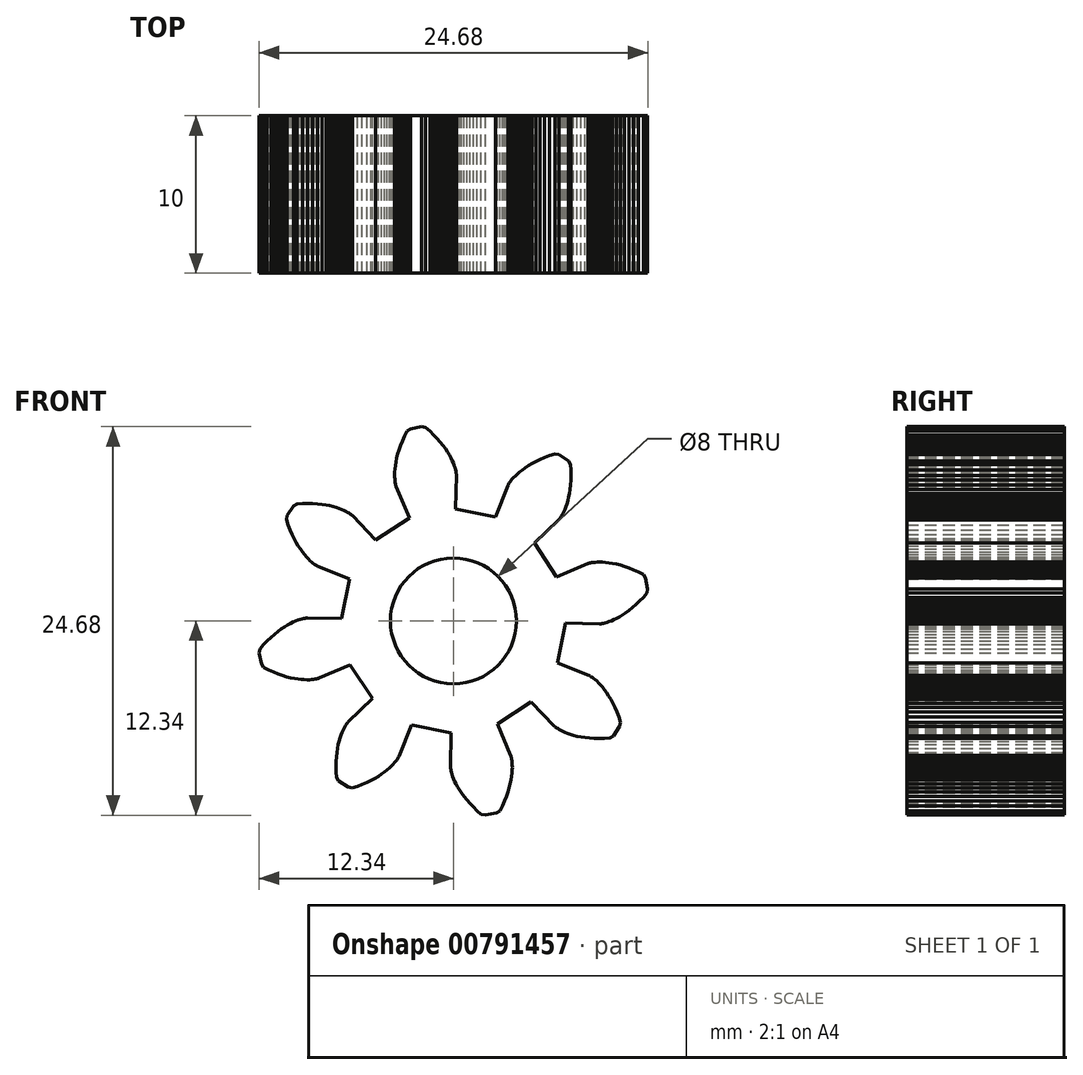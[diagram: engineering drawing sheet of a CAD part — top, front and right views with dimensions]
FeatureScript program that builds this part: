
annotation { "Feature Type Name" : "Feature", "Feature Type Description" : "" }
export const myFeature = defineFeature(function(context is Context, id is Id, definition is map)
    precondition{}
    {
        {
            var Q0;
            Q0=qCreatedBy(makeId("Front.planeOp"),FACE);
            var sketch = newSketch(context, id + "F0", { "sketchPlane" : qUnion([Q0])});
            skCircle(sketch, "E0", {"center": v(0, 0) * mm, "radius": 4 * mm});
            skLineSegment(sketch, "E1", {"start": v(-7.12, 0.14) * mm, "end": v(-9.27, 0.19) * mm});
            skLineSegment(sketch, "E2", {"start": v(-9.27, 0.19) * mm, "end": v(-9.29, 0.19) * mm});
            skLineSegment(sketch, "E3", {"start": v(-9.29, 0.19) * mm, "end": v(-9.32, 0.18) * mm});
            skLineSegment(sketch, "E4", {"start": v(-9.32, 0.18) * mm, "end": v(-9.37, 0.18) * mm});
            skLineSegment(sketch, "E5", {"start": v(-9.37, 0.18) * mm, "end": v(-9.44, 0.17) * mm});
            skLineSegment(sketch, "E6", {"start": v(-9.44, 0.17) * mm, "end": v(-9.52, 0.15) * mm});
            skLineSegment(sketch, "E7", {"start": v(-9.52, 0.15) * mm, "end": v(-9.63, 0.13) * mm});
            skLineSegment(sketch, "E8", {"start": v(-9.63, 0.13) * mm, "end": v(-9.74, 0.1) * mm});
            skLineSegment(sketch, "E9", {"start": v(-9.74, 0.1) * mm, "end": v(-9.87, 0.05) * mm});
            skLineSegment(sketch, "E10", {"start": v(-9.87, 0.05) * mm, "end": v(-10.02, 0) * mm});
            skLineSegment(sketch, "E11", {"start": v(-10.02, 0) * mm, "end": v(-10.18, -0.08) * mm});
            skLineSegment(sketch, "E12", {"start": v(-10.18, -0.08) * mm, "end": v(-10.35, -0.16) * mm});
            skLineSegment(sketch, "E13", {"start": v(-10.35, -0.16) * mm, "end": v(-10.54, -0.26) * mm});
            skLineSegment(sketch, "E14", {"start": v(-10.54, -0.26) * mm, "end": v(-10.73, -0.38) * mm});
            skLineSegment(sketch, "E15", {"start": v(-10.73, -0.38) * mm, "end": v(-10.94, -0.52) * mm});
            skLineSegment(sketch, "E16", {"start": v(-10.94, -0.52) * mm, "end": v(-11.15, -0.67) * mm});
            skLineSegment(sketch, "E17", {"start": v(-11.15, -0.67) * mm, "end": v(-11.37, -0.85) * mm});
            skLineSegment(sketch, "E18", {"start": v(-11.37, -0.85) * mm, "end": v(-11.6, -1.04) * mm});
            skLineSegment(sketch, "E19", {"start": v(-11.6, -1.04) * mm, "end": v(-11.82, -1.26) * mm});
            skLineSegment(sketch, "E20", {"start": v(-11.82, -1.26) * mm, "end": v(-12.05, -1.5) * mm});
            skLineSegment(sketch, "E21", {"start": v(-12.05, -1.5) * mm, "end": v(-12.29, -1.77) * mm});
            skLineSegment(sketch, "E22", {"start": v(-12.29, -1.77) * mm, "end": v(-12.34, -2.02) * mm});
            skLineSegment(sketch, "E23", {"start": v(-12.34, -2.02) * mm, "end": v(-12.2, -2.73) * mm});
            skLineSegment(sketch, "E24", {"start": v(-12.2, -2.73) * mm, "end": v(-12.06, -2.95) * mm});
            skLineSegment(sketch, "E25", {"start": v(-12.06, -2.95) * mm, "end": v(-11.74, -3.11) * mm});
            skLineSegment(sketch, "E26", {"start": v(-11.74, -3.11) * mm, "end": v(-11.44, -3.25) * mm});
            skLineSegment(sketch, "E27", {"start": v(-11.44, -3.25) * mm, "end": v(-11.14, -3.36) * mm});
            skLineSegment(sketch, "E28", {"start": v(-11.14, -3.36) * mm, "end": v(-10.86, -3.46) * mm});
            skLineSegment(sketch, "E29", {"start": v(-10.86, -3.46) * mm, "end": v(-10.6, -3.54) * mm});
            skLineSegment(sketch, "E30", {"start": v(-10.6, -3.54) * mm, "end": v(-10.34, -3.6) * mm});
            skLineSegment(sketch, "E31", {"start": v(-10.34, -3.6) * mm, "end": v(-10.1, -3.66) * mm});
            skLineSegment(sketch, "E32", {"start": v(-10.1, -3.66) * mm, "end": v(-9.87, -3.7) * mm});
            skLineSegment(sketch, "E33", {"start": v(-9.87, -3.7) * mm, "end": v(-9.67, -3.72) * mm});
            skLineSegment(sketch, "E34", {"start": v(-9.67, -3.72) * mm, "end": v(-9.47, -3.73) * mm});
            skLineSegment(sketch, "E35", {"start": v(-9.47, -3.73) * mm, "end": v(-9.3, -3.74) * mm});
            skLineSegment(sketch, "E36", {"start": v(-9.3, -3.74) * mm, "end": v(-9.14, -3.73) * mm});
            skLineSegment(sketch, "E37", {"start": v(-9.14, -3.73) * mm, "end": v(-9, -3.73) * mm});
            skLineSegment(sketch, "E38", {"start": v(-9, -3.73) * mm, "end": v(-8.88, -3.71) * mm});
            skLineSegment(sketch, "E39", {"start": v(-8.88, -3.71) * mm, "end": v(-8.78, -3.7) * mm});
            skLineSegment(sketch, "E40", {"start": v(-8.78, -3.7) * mm, "end": v(-8.7, -3.68) * mm});
            skLineSegment(sketch, "E41", {"start": v(-8.7, -3.68) * mm, "end": v(-8.63, -3.67) * mm});
            skLineSegment(sketch, "E42", {"start": v(-8.63, -3.67) * mm, "end": v(-8.58, -3.65) * mm});
            skLineSegment(sketch, "E43", {"start": v(-8.58, -3.65) * mm, "end": v(-8.55, -3.64) * mm});
            skLineSegment(sketch, "E44", {"start": v(-8.55, -3.64) * mm, "end": v(-8.53, -3.64) * mm});
            skLineSegment(sketch, "E45", {"start": v(-8.53, -3.64) * mm, "end": v(-6.55, -2.8) * mm});
            skLineSegment(sketch, "E46", {"start": v(-6.55, -2.8) * mm, "end": v(-5.14, -4.94) * mm});
            skLineSegment(sketch, "E47", {"start": v(-5.14, -4.94) * mm, "end": v(-6.69, -6.42) * mm});
            skLineSegment(sketch, "E48", {"start": v(-6.69, -6.42) * mm, "end": v(-6.7, -6.44) * mm});
            skLineSegment(sketch, "E49", {"start": v(-6.7, -6.44) * mm, "end": v(-6.72, -6.46) * mm});
            skLineSegment(sketch, "E50", {"start": v(-6.72, -6.46) * mm, "end": v(-6.75, -6.5) * mm});
            skLineSegment(sketch, "E51", {"start": v(-6.75, -6.5) * mm, "end": v(-6.8, -6.56) * mm});
            skLineSegment(sketch, "E52", {"start": v(-6.8, -6.56) * mm, "end": v(-6.84, -6.63) * mm});
            skLineSegment(sketch, "E53", {"start": v(-6.84, -6.63) * mm, "end": v(-6.9, -6.72) * mm});
            skLineSegment(sketch, "E54", {"start": v(-6.9, -6.72) * mm, "end": v(-6.95, -6.82) * mm});
            skLineSegment(sketch, "E55", {"start": v(-6.95, -6.82) * mm, "end": v(-7.02, -6.95) * mm});
            skLineSegment(sketch, "E56", {"start": v(-7.02, -6.95) * mm, "end": v(-7.08, -7.1) * mm});
            skLineSegment(sketch, "E57", {"start": v(-7.08, -7.1) * mm, "end": v(-7.14, -7.25) * mm});
            skLineSegment(sketch, "E58", {"start": v(-7.14, -7.25) * mm, "end": v(-7.2, -7.44) * mm});
            skLineSegment(sketch, "E59", {"start": v(-7.2, -7.44) * mm, "end": v(-7.27, -7.64) * mm});
            skLineSegment(sketch, "E60", {"start": v(-7.27, -7.64) * mm, "end": v(-7.32, -7.86) * mm});
            skLineSegment(sketch, "E61", {"start": v(-7.32, -7.86) * mm, "end": v(-7.37, -8.1) * mm});
            skLineSegment(sketch, "E62", {"start": v(-7.37, -8.1) * mm, "end": v(-7.4, -8.36) * mm});
            skLineSegment(sketch, "E63", {"start": v(-7.4, -8.36) * mm, "end": v(-7.44, -8.64) * mm});
            skLineSegment(sketch, "E64", {"start": v(-7.44, -8.64) * mm, "end": v(-7.46, -8.94) * mm});
            skLineSegment(sketch, "E65", {"start": v(-7.46, -8.94) * mm, "end": v(-7.47, -9.25) * mm});
            skLineSegment(sketch, "E66", {"start": v(-7.47, -9.25) * mm, "end": v(-7.46, -9.59) * mm});
            skLineSegment(sketch, "E67", {"start": v(-7.46, -9.59) * mm, "end": v(-7.44, -9.94) * mm});
            skLineSegment(sketch, "E68", {"start": v(-7.44, -9.94) * mm, "end": v(-7.3, -10.15) * mm});
            skLineSegment(sketch, "E69", {"start": v(-7.3, -10.15) * mm, "end": v(-6.7, -10.56) * mm});
            skLineSegment(sketch, "E70", {"start": v(-6.7, -10.56) * mm, "end": v(-6.44, -10.61) * mm});
            skLineSegment(sketch, "E71", {"start": v(-6.44, -10.61) * mm, "end": v(-6.1, -10.5) * mm});
            skLineSegment(sketch, "E72", {"start": v(-6.1, -10.5) * mm, "end": v(-5.8, -10.38) * mm});
            skLineSegment(sketch, "E73", {"start": v(-5.8, -10.38) * mm, "end": v(-5.5, -10.26) * mm});
            skLineSegment(sketch, "E74", {"start": v(-5.5, -10.26) * mm, "end": v(-5.23, -10.13) * mm});
            skLineSegment(sketch, "E75", {"start": v(-5.23, -10.13) * mm, "end": v(-4.99, -10) * mm});
            skLineSegment(sketch, "E76", {"start": v(-4.99, -10) * mm, "end": v(-4.76, -9.86) * mm});
            skLineSegment(sketch, "E77", {"start": v(-4.76, -9.86) * mm, "end": v(-4.56, -9.73) * mm});
            skLineSegment(sketch, "E78", {"start": v(-4.56, -9.73) * mm, "end": v(-4.37, -9.6) * mm});
            skLineSegment(sketch, "E79", {"start": v(-4.37, -9.6) * mm, "end": v(-4.2, -9.46) * mm});
            skLineSegment(sketch, "E80", {"start": v(-4.2, -9.46) * mm, "end": v(-4.06, -9.34) * mm});
            skLineSegment(sketch, "E81", {"start": v(-4.06, -9.34) * mm, "end": v(-3.93, -9.22) * mm});
            skLineSegment(sketch, "E82", {"start": v(-3.93, -9.22) * mm, "end": v(-3.82, -9.1) * mm});
            skLineSegment(sketch, "E83", {"start": v(-3.82, -9.1) * mm, "end": v(-3.73, -9) * mm});
            skLineSegment(sketch, "E84", {"start": v(-3.73, -9) * mm, "end": v(-3.65, -8.9) * mm});
            skLineSegment(sketch, "E85", {"start": v(-3.65, -8.9) * mm, "end": v(-3.6, -8.82) * mm});
            skLineSegment(sketch, "E86", {"start": v(-3.6, -8.82) * mm, "end": v(-3.54, -8.75) * mm});
            skLineSegment(sketch, "E87", {"start": v(-3.54, -8.75) * mm, "end": v(-3.5, -8.7) * mm});
            skLineSegment(sketch, "E88", {"start": v(-3.5, -8.7) * mm, "end": v(-3.48, -8.65) * mm});
            skLineSegment(sketch, "E89", {"start": v(-3.48, -8.65) * mm, "end": v(-3.47, -8.62) * mm});
            skLineSegment(sketch, "E90", {"start": v(-3.47, -8.62) * mm, "end": v(-3.46, -8.6) * mm});
            skLineSegment(sketch, "E91", {"start": v(-3.46, -8.6) * mm, "end": v(-2.66, -6.61) * mm});
            skLineSegment(sketch, "E92", {"start": v(-2.66, -6.61) * mm, "end": v(-0.14, -7.12) * mm});
            skLineSegment(sketch, "E93", {"start": v(-0.14, -7.12) * mm, "end": v(-0.19, -9.27) * mm});
            skLineSegment(sketch, "E94", {"start": v(-0.19, -9.27) * mm, "end": v(-0.19, -9.29) * mm});
            skLineSegment(sketch, "E95", {"start": v(-0.19, -9.29) * mm, "end": v(-0.18, -9.32) * mm});
            skLineSegment(sketch, "E96", {"start": v(-0.18, -9.32) * mm, "end": v(-0.18, -9.37) * mm});
            skLineSegment(sketch, "E97", {"start": v(-0.18, -9.37) * mm, "end": v(-0.17, -9.44) * mm});
            skLineSegment(sketch, "E98", {"start": v(-0.17, -9.44) * mm, "end": v(-0.15, -9.52) * mm});
            skLineSegment(sketch, "E99", {"start": v(-0.15, -9.52) * mm, "end": v(-0.13, -9.63) * mm});
            skLineSegment(sketch, "E100", {"start": v(-0.13, -9.63) * mm, "end": v(-0.1, -9.74) * mm});
            skLineSegment(sketch, "E101", {"start": v(-0.1, -9.74) * mm, "end": v(-0.05, -9.87) * mm});
            skLineSegment(sketch, "E102", {"start": v(-0.05, -9.87) * mm, "end": v(0, -10.02) * mm});
            skLineSegment(sketch, "E103", {"start": v(0, -10.02) * mm, "end": v(0.08, -10.18) * mm});
            skLineSegment(sketch, "E104", {"start": v(0.08, -10.18) * mm, "end": v(0.16, -10.35) * mm});
            skLineSegment(sketch, "E105", {"start": v(0.16, -10.35) * mm, "end": v(0.26, -10.54) * mm});
            skLineSegment(sketch, "E106", {"start": v(0.26, -10.54) * mm, "end": v(0.38, -10.73) * mm});
            skLineSegment(sketch, "E107", {"start": v(0.38, -10.73) * mm, "end": v(0.52, -10.94) * mm});
            skLineSegment(sketch, "E108", {"start": v(0.52, -10.94) * mm, "end": v(0.67, -11.15) * mm});
            skLineSegment(sketch, "E109", {"start": v(0.67, -11.15) * mm, "end": v(0.85, -11.37) * mm});
            skLineSegment(sketch, "E110", {"start": v(0.85, -11.37) * mm, "end": v(1.04, -11.6) * mm});
            skLineSegment(sketch, "E111", {"start": v(1.04, -11.6) * mm, "end": v(1.26, -11.82) * mm});
            skLineSegment(sketch, "E112", {"start": v(1.26, -11.82) * mm, "end": v(1.5, -12.05) * mm});
            skLineSegment(sketch, "E113", {"start": v(1.5, -12.05) * mm, "end": v(1.77, -12.29) * mm});
            skLineSegment(sketch, "E114", {"start": v(1.77, -12.29) * mm, "end": v(2.02, -12.34) * mm});
            skLineSegment(sketch, "E115", {"start": v(2.02, -12.34) * mm, "end": v(2.73, -12.2) * mm});
            skLineSegment(sketch, "E116", {"start": v(2.73, -12.2) * mm, "end": v(2.95, -12.06) * mm});
            skLineSegment(sketch, "E117", {"start": v(2.95, -12.06) * mm, "end": v(3.11, -11.74) * mm});
            skLineSegment(sketch, "E118", {"start": v(3.11, -11.74) * mm, "end": v(3.25, -11.44) * mm});
            skLineSegment(sketch, "E119", {"start": v(3.25, -11.44) * mm, "end": v(3.36, -11.14) * mm});
            skLineSegment(sketch, "E120", {"start": v(3.36, -11.14) * mm, "end": v(3.46, -10.86) * mm});
            skLineSegment(sketch, "E121", {"start": v(3.46, -10.86) * mm, "end": v(3.54, -10.6) * mm});
            skLineSegment(sketch, "E122", {"start": v(3.54, -10.6) * mm, "end": v(3.6, -10.34) * mm});
            skLineSegment(sketch, "E123", {"start": v(3.6, -10.34) * mm, "end": v(3.66, -10.1) * mm});
            skLineSegment(sketch, "E124", {"start": v(3.66, -10.1) * mm, "end": v(3.7, -9.87) * mm});
            skLineSegment(sketch, "E125", {"start": v(3.7, -9.87) * mm, "end": v(3.72, -9.67) * mm});
            skLineSegment(sketch, "E126", {"start": v(3.72, -9.67) * mm, "end": v(3.73, -9.47) * mm});
            skLineSegment(sketch, "E127", {"start": v(3.73, -9.47) * mm, "end": v(3.74, -9.3) * mm});
            skLineSegment(sketch, "E128", {"start": v(3.74, -9.3) * mm, "end": v(3.73, -9.14) * mm});
            skLineSegment(sketch, "E129", {"start": v(3.73, -9.14) * mm, "end": v(3.73, -9) * mm});
            skLineSegment(sketch, "E130", {"start": v(3.73, -9) * mm, "end": v(3.71, -8.88) * mm});
            skLineSegment(sketch, "E131", {"start": v(3.71, -8.88) * mm, "end": v(3.7, -8.78) * mm});
            skLineSegment(sketch, "E132", {"start": v(3.7, -8.78) * mm, "end": v(3.68, -8.7) * mm});
            skLineSegment(sketch, "E133", {"start": v(3.68, -8.7) * mm, "end": v(3.67, -8.63) * mm});
            skLineSegment(sketch, "E134", {"start": v(3.67, -8.63) * mm, "end": v(3.65, -8.58) * mm});
            skLineSegment(sketch, "E135", {"start": v(3.65, -8.58) * mm, "end": v(3.64, -8.55) * mm});
            skLineSegment(sketch, "E136", {"start": v(3.64, -8.55) * mm, "end": v(3.64, -8.53) * mm});
            skLineSegment(sketch, "E137", {"start": v(3.64, -8.53) * mm, "end": v(2.8, -6.55) * mm});
            skLineSegment(sketch, "E138", {"start": v(2.8, -6.55) * mm, "end": v(4.94, -5.14) * mm});
            skLineSegment(sketch, "E139", {"start": v(4.94, -5.14) * mm, "end": v(6.42, -6.69) * mm});
            skLineSegment(sketch, "E140", {"start": v(6.42, -6.69) * mm, "end": v(6.44, -6.7) * mm});
            skLineSegment(sketch, "E141", {"start": v(6.44, -6.7) * mm, "end": v(6.46, -6.72) * mm});
            skLineSegment(sketch, "E142", {"start": v(6.46, -6.72) * mm, "end": v(6.5, -6.75) * mm});
            skLineSegment(sketch, "E143", {"start": v(6.5, -6.75) * mm, "end": v(6.56, -6.8) * mm});
            skLineSegment(sketch, "E144", {"start": v(6.56, -6.8) * mm, "end": v(6.63, -6.84) * mm});
            skLineSegment(sketch, "E145", {"start": v(6.63, -6.84) * mm, "end": v(6.72, -6.9) * mm});
            skLineSegment(sketch, "E146", {"start": v(6.72, -6.9) * mm, "end": v(6.82, -6.95) * mm});
            skLineSegment(sketch, "E147", {"start": v(6.82, -6.95) * mm, "end": v(6.95, -7.02) * mm});
            skLineSegment(sketch, "E148", {"start": v(6.95, -7.02) * mm, "end": v(7.1, -7.08) * mm});
            skLineSegment(sketch, "E149", {"start": v(7.1, -7.08) * mm, "end": v(7.25, -7.14) * mm});
            skLineSegment(sketch, "E150", {"start": v(7.25, -7.14) * mm, "end": v(7.44, -7.2) * mm});
            skLineSegment(sketch, "E151", {"start": v(7.44, -7.2) * mm, "end": v(7.64, -7.27) * mm});
            skLineSegment(sketch, "E152", {"start": v(7.64, -7.27) * mm, "end": v(7.86, -7.32) * mm});
            skLineSegment(sketch, "E153", {"start": v(7.86, -7.32) * mm, "end": v(8.1, -7.37) * mm});
            skLineSegment(sketch, "E154", {"start": v(8.1, -7.37) * mm, "end": v(8.36, -7.4) * mm});
            skLineSegment(sketch, "E155", {"start": v(8.36, -7.4) * mm, "end": v(8.64, -7.44) * mm});
            skLineSegment(sketch, "E156", {"start": v(8.64, -7.44) * mm, "end": v(8.94, -7.46) * mm});
            skLineSegment(sketch, "E157", {"start": v(8.94, -7.46) * mm, "end": v(9.25, -7.47) * mm});
            skLineSegment(sketch, "E158", {"start": v(9.25, -7.47) * mm, "end": v(9.59, -7.46) * mm});
            skLineSegment(sketch, "E159", {"start": v(9.59, -7.46) * mm, "end": v(9.94, -7.44) * mm});
            skLineSegment(sketch, "E160", {"start": v(9.94, -7.44) * mm, "end": v(10.15, -7.3) * mm});
            skLineSegment(sketch, "E161", {"start": v(10.15, -7.3) * mm, "end": v(10.56, -6.7) * mm});
            skLineSegment(sketch, "E162", {"start": v(10.56, -6.7) * mm, "end": v(10.61, -6.44) * mm});
            skLineSegment(sketch, "E163", {"start": v(10.61, -6.44) * mm, "end": v(10.5, -6.1) * mm});
            skLineSegment(sketch, "E164", {"start": v(10.5, -6.1) * mm, "end": v(10.38, -5.8) * mm});
            skLineSegment(sketch, "E165", {"start": v(10.38, -5.8) * mm, "end": v(10.26, -5.5) * mm});
            skLineSegment(sketch, "E166", {"start": v(10.26, -5.5) * mm, "end": v(10.13, -5.23) * mm});
            skLineSegment(sketch, "E167", {"start": v(10.13, -5.23) * mm, "end": v(10, -4.99) * mm});
            skLineSegment(sketch, "E168", {"start": v(10, -4.99) * mm, "end": v(9.86, -4.76) * mm});
            skLineSegment(sketch, "E169", {"start": v(9.86, -4.76) * mm, "end": v(9.73, -4.56) * mm});
            skLineSegment(sketch, "E170", {"start": v(9.73, -4.56) * mm, "end": v(9.6, -4.37) * mm});
            skLineSegment(sketch, "E171", {"start": v(9.6, -4.37) * mm, "end": v(9.46, -4.2) * mm});
            skLineSegment(sketch, "E172", {"start": v(9.46, -4.2) * mm, "end": v(9.34, -4.06) * mm});
            skLineSegment(sketch, "E173", {"start": v(9.34, -4.06) * mm, "end": v(9.22, -3.93) * mm});
            skLineSegment(sketch, "E174", {"start": v(9.22, -3.93) * mm, "end": v(9.1, -3.82) * mm});
            skLineSegment(sketch, "E175", {"start": v(9.1, -3.82) * mm, "end": v(9, -3.73) * mm});
            skLineSegment(sketch, "E176", {"start": v(9, -3.73) * mm, "end": v(8.9, -3.65) * mm});
            skLineSegment(sketch, "E177", {"start": v(8.9, -3.65) * mm, "end": v(8.82, -3.6) * mm});
            skLineSegment(sketch, "E178", {"start": v(8.82, -3.6) * mm, "end": v(8.75, -3.54) * mm});
            skLineSegment(sketch, "E179", {"start": v(8.75, -3.54) * mm, "end": v(8.7, -3.5) * mm});
            skLineSegment(sketch, "E180", {"start": v(8.7, -3.5) * mm, "end": v(8.65, -3.48) * mm});
            skLineSegment(sketch, "E181", {"start": v(8.65, -3.48) * mm, "end": v(8.62, -3.47) * mm});
            skLineSegment(sketch, "E182", {"start": v(8.62, -3.47) * mm, "end": v(8.6, -3.46) * mm});
            skLineSegment(sketch, "E183", {"start": v(8.6, -3.46) * mm, "end": v(6.61, -2.66) * mm});
            skLineSegment(sketch, "E184", {"start": v(6.61, -2.66) * mm, "end": v(7.12, -0.14) * mm});
            skLineSegment(sketch, "E185", {"start": v(7.12, -0.14) * mm, "end": v(9.27, -0.19) * mm});
            skLineSegment(sketch, "E186", {"start": v(9.27, -0.19) * mm, "end": v(9.29, -0.19) * mm});
            skLineSegment(sketch, "E187", {"start": v(9.29, -0.19) * mm, "end": v(9.32, -0.18) * mm});
            skLineSegment(sketch, "E188", {"start": v(9.32, -0.18) * mm, "end": v(9.37, -0.18) * mm});
            skLineSegment(sketch, "E189", {"start": v(9.37, -0.18) * mm, "end": v(9.44, -0.17) * mm});
            skLineSegment(sketch, "E190", {"start": v(9.44, -0.17) * mm, "end": v(9.52, -0.15) * mm});
            skLineSegment(sketch, "E191", {"start": v(9.52, -0.15) * mm, "end": v(9.63, -0.13) * mm});
            skLineSegment(sketch, "E192", {"start": v(9.63, -0.13) * mm, "end": v(9.74, -0.1) * mm});
            skLineSegment(sketch, "E193", {"start": v(9.74, -0.1) * mm, "end": v(9.87, -0.05) * mm});
            skLineSegment(sketch, "E194", {"start": v(9.87, -0.05) * mm, "end": v(10.02, 0) * mm});
            skLineSegment(sketch, "E195", {"start": v(10.02, 0) * mm, "end": v(10.18, 0.08) * mm});
            skLineSegment(sketch, "E196", {"start": v(10.18, 0.08) * mm, "end": v(10.35, 0.16) * mm});
            skLineSegment(sketch, "E197", {"start": v(10.35, 0.16) * mm, "end": v(10.54, 0.26) * mm});
            skLineSegment(sketch, "E198", {"start": v(10.54, 0.26) * mm, "end": v(10.73, 0.38) * mm});
            skLineSegment(sketch, "E199", {"start": v(10.73, 0.38) * mm, "end": v(10.94, 0.52) * mm});
            skLineSegment(sketch, "E200", {"start": v(10.94, 0.52) * mm, "end": v(11.15, 0.67) * mm});
            skLineSegment(sketch, "E201", {"start": v(11.15, 0.67) * mm, "end": v(11.37, 0.85) * mm});
            skLineSegment(sketch, "E202", {"start": v(11.37, 0.85) * mm, "end": v(11.6, 1.04) * mm});
            skLineSegment(sketch, "E203", {"start": v(11.6, 1.04) * mm, "end": v(11.82, 1.26) * mm});
            skLineSegment(sketch, "E204", {"start": v(11.82, 1.26) * mm, "end": v(12.05, 1.5) * mm});
            skLineSegment(sketch, "E205", {"start": v(12.05, 1.5) * mm, "end": v(12.29, 1.77) * mm});
            skLineSegment(sketch, "E206", {"start": v(12.29, 1.77) * mm, "end": v(12.34, 2.02) * mm});
            skLineSegment(sketch, "E207", {"start": v(12.34, 2.02) * mm, "end": v(12.2, 2.73) * mm});
            skLineSegment(sketch, "E208", {"start": v(12.2, 2.73) * mm, "end": v(12.06, 2.95) * mm});
            skLineSegment(sketch, "E209", {"start": v(12.06, 2.95) * mm, "end": v(11.74, 3.11) * mm});
            skLineSegment(sketch, "E210", {"start": v(11.74, 3.11) * mm, "end": v(11.44, 3.25) * mm});
            skLineSegment(sketch, "E211", {"start": v(11.44, 3.25) * mm, "end": v(11.14, 3.36) * mm});
            skLineSegment(sketch, "E212", {"start": v(11.14, 3.36) * mm, "end": v(10.86, 3.46) * mm});
            skLineSegment(sketch, "E213", {"start": v(10.86, 3.46) * mm, "end": v(10.6, 3.54) * mm});
            skLineSegment(sketch, "E214", {"start": v(10.6, 3.54) * mm, "end": v(10.34, 3.6) * mm});
            skLineSegment(sketch, "E215", {"start": v(10.34, 3.6) * mm, "end": v(10.1, 3.66) * mm});
            skLineSegment(sketch, "E216", {"start": v(10.1, 3.66) * mm, "end": v(9.87, 3.7) * mm});
            skLineSegment(sketch, "E217", {"start": v(9.87, 3.7) * mm, "end": v(9.67, 3.72) * mm});
            skLineSegment(sketch, "E218", {"start": v(9.67, 3.72) * mm, "end": v(9.47, 3.73) * mm});
            skLineSegment(sketch, "E219", {"start": v(9.47, 3.73) * mm, "end": v(9.3, 3.74) * mm});
            skLineSegment(sketch, "E220", {"start": v(9.3, 3.74) * mm, "end": v(9.14, 3.73) * mm});
            skLineSegment(sketch, "E221", {"start": v(9.14, 3.73) * mm, "end": v(9, 3.73) * mm});
            skLineSegment(sketch, "E222", {"start": v(9, 3.73) * mm, "end": v(8.88, 3.71) * mm});
            skLineSegment(sketch, "E223", {"start": v(8.88, 3.71) * mm, "end": v(8.78, 3.7) * mm});
            skLineSegment(sketch, "E224", {"start": v(8.78, 3.7) * mm, "end": v(8.7, 3.68) * mm});
            skLineSegment(sketch, "E225", {"start": v(8.7, 3.68) * mm, "end": v(8.63, 3.67) * mm});
            skLineSegment(sketch, "E226", {"start": v(8.63, 3.67) * mm, "end": v(8.58, 3.65) * mm});
            skLineSegment(sketch, "E227", {"start": v(8.58, 3.65) * mm, "end": v(8.55, 3.64) * mm});
            skLineSegment(sketch, "E228", {"start": v(8.55, 3.64) * mm, "end": v(8.53, 3.64) * mm});
            skLineSegment(sketch, "E229", {"start": v(8.53, 3.64) * mm, "end": v(6.55, 2.8) * mm});
            skLineSegment(sketch, "E230", {"start": v(6.55, 2.8) * mm, "end": v(5.14, 4.94) * mm});
            skLineSegment(sketch, "E231", {"start": v(5.14, 4.94) * mm, "end": v(6.69, 6.42) * mm});
            skLineSegment(sketch, "E232", {"start": v(6.69, 6.42) * mm, "end": v(6.7, 6.44) * mm});
            skLineSegment(sketch, "E233", {"start": v(6.7, 6.44) * mm, "end": v(6.72, 6.46) * mm});
            skLineSegment(sketch, "E234", {"start": v(6.72, 6.46) * mm, "end": v(6.75, 6.5) * mm});
            skLineSegment(sketch, "E235", {"start": v(6.75, 6.5) * mm, "end": v(6.8, 6.56) * mm});
            skLineSegment(sketch, "E236", {"start": v(6.8, 6.56) * mm, "end": v(6.84, 6.63) * mm});
            skLineSegment(sketch, "E237", {"start": v(6.84, 6.63) * mm, "end": v(6.9, 6.72) * mm});
            skLineSegment(sketch, "E238", {"start": v(6.9, 6.72) * mm, "end": v(6.95, 6.82) * mm});
            skLineSegment(sketch, "E239", {"start": v(6.95, 6.82) * mm, "end": v(7.02, 6.95) * mm});
            skLineSegment(sketch, "E240", {"start": v(7.02, 6.95) * mm, "end": v(7.08, 7.1) * mm});
            skLineSegment(sketch, "E241", {"start": v(7.08, 7.1) * mm, "end": v(7.14, 7.25) * mm});
            skLineSegment(sketch, "E242", {"start": v(7.14, 7.25) * mm, "end": v(7.2, 7.44) * mm});
            skLineSegment(sketch, "E243", {"start": v(7.2, 7.44) * mm, "end": v(7.27, 7.64) * mm});
            skLineSegment(sketch, "E244", {"start": v(7.27, 7.64) * mm, "end": v(7.32, 7.86) * mm});
            skLineSegment(sketch, "E245", {"start": v(7.32, 7.86) * mm, "end": v(7.37, 8.1) * mm});
            skLineSegment(sketch, "E246", {"start": v(7.37, 8.1) * mm, "end": v(7.4, 8.36) * mm});
            skLineSegment(sketch, "E247", {"start": v(7.4, 8.36) * mm, "end": v(7.44, 8.64) * mm});
            skLineSegment(sketch, "E248", {"start": v(7.44, 8.64) * mm, "end": v(7.46, 8.94) * mm});
            skLineSegment(sketch, "E249", {"start": v(7.46, 8.94) * mm, "end": v(7.47, 9.25) * mm});
            skLineSegment(sketch, "E250", {"start": v(7.47, 9.25) * mm, "end": v(7.46, 9.59) * mm});
            skLineSegment(sketch, "E251", {"start": v(7.46, 9.59) * mm, "end": v(7.44, 9.94) * mm});
            skLineSegment(sketch, "E252", {"start": v(7.44, 9.94) * mm, "end": v(7.3, 10.15) * mm});
            skLineSegment(sketch, "E253", {"start": v(7.3, 10.15) * mm, "end": v(6.7, 10.56) * mm});
            skLineSegment(sketch, "E254", {"start": v(6.7, 10.56) * mm, "end": v(6.44, 10.61) * mm});
            skLineSegment(sketch, "E255", {"start": v(6.44, 10.61) * mm, "end": v(6.1, 10.5) * mm});
            skLineSegment(sketch, "E256", {"start": v(6.1, 10.5) * mm, "end": v(5.8, 10.38) * mm});
            skLineSegment(sketch, "E257", {"start": v(5.8, 10.38) * mm, "end": v(5.5, 10.26) * mm});
            skLineSegment(sketch, "E258", {"start": v(5.5, 10.26) * mm, "end": v(5.23, 10.13) * mm});
            skLineSegment(sketch, "E259", {"start": v(5.23, 10.13) * mm, "end": v(4.99, 10) * mm});
            skLineSegment(sketch, "E260", {"start": v(4.99, 10) * mm, "end": v(4.76, 9.86) * mm});
            skLineSegment(sketch, "E261", {"start": v(4.76, 9.86) * mm, "end": v(4.56, 9.73) * mm});
            skLineSegment(sketch, "E262", {"start": v(4.56, 9.73) * mm, "end": v(4.37, 9.6) * mm});
            skLineSegment(sketch, "E263", {"start": v(4.37, 9.6) * mm, "end": v(4.2, 9.46) * mm});
            skLineSegment(sketch, "E264", {"start": v(4.2, 9.46) * mm, "end": v(4.06, 9.34) * mm});
            skLineSegment(sketch, "E265", {"start": v(4.06, 9.34) * mm, "end": v(3.93, 9.22) * mm});
            skLineSegment(sketch, "E266", {"start": v(3.93, 9.22) * mm, "end": v(3.82, 9.1) * mm});
            skLineSegment(sketch, "E267", {"start": v(3.82, 9.1) * mm, "end": v(3.73, 9) * mm});
            skLineSegment(sketch, "E268", {"start": v(3.73, 9) * mm, "end": v(3.65, 8.9) * mm});
            skLineSegment(sketch, "E269", {"start": v(3.65, 8.9) * mm, "end": v(3.6, 8.82) * mm});
            skLineSegment(sketch, "E270", {"start": v(3.6, 8.82) * mm, "end": v(3.54, 8.75) * mm});
            skLineSegment(sketch, "E271", {"start": v(3.54, 8.75) * mm, "end": v(3.5, 8.7) * mm});
            skLineSegment(sketch, "E272", {"start": v(3.5, 8.7) * mm, "end": v(3.48, 8.65) * mm});
            skLineSegment(sketch, "E273", {"start": v(3.48, 8.65) * mm, "end": v(3.47, 8.62) * mm});
            skLineSegment(sketch, "E274", {"start": v(3.47, 8.62) * mm, "end": v(3.46, 8.6) * mm});
            skLineSegment(sketch, "E275", {"start": v(3.46, 8.6) * mm, "end": v(2.66, 6.61) * mm});
            skLineSegment(sketch, "E276", {"start": v(2.66, 6.61) * mm, "end": v(0.14, 7.12) * mm});
            skLineSegment(sketch, "E277", {"start": v(0.14, 7.12) * mm, "end": v(0.19, 9.27) * mm});
            skLineSegment(sketch, "E278", {"start": v(0.19, 9.27) * mm, "end": v(0.19, 9.29) * mm});
            skLineSegment(sketch, "E279", {"start": v(0.19, 9.29) * mm, "end": v(0.18, 9.32) * mm});
            skLineSegment(sketch, "E280", {"start": v(0.18, 9.32) * mm, "end": v(0.18, 9.37) * mm});
            skLineSegment(sketch, "E281", {"start": v(0.18, 9.37) * mm, "end": v(0.17, 9.44) * mm});
            skLineSegment(sketch, "E282", {"start": v(0.17, 9.44) * mm, "end": v(0.15, 9.52) * mm});
            skLineSegment(sketch, "E283", {"start": v(0.15, 9.52) * mm, "end": v(0.13, 9.63) * mm});
            skLineSegment(sketch, "E284", {"start": v(0.13, 9.63) * mm, "end": v(0.1, 9.74) * mm});
            skLineSegment(sketch, "E285", {"start": v(0.1, 9.74) * mm, "end": v(0.05, 9.87) * mm});
            skLineSegment(sketch, "E286", {"start": v(0.05, 9.87) * mm, "end": v(0, 10.02) * mm});
            skLineSegment(sketch, "E287", {"start": v(0, 10.02) * mm, "end": v(-0.08, 10.18) * mm});
            skLineSegment(sketch, "E288", {"start": v(-0.08, 10.18) * mm, "end": v(-0.16, 10.35) * mm});
            skLineSegment(sketch, "E289", {"start": v(-0.16, 10.35) * mm, "end": v(-0.26, 10.54) * mm});
            skLineSegment(sketch, "E290", {"start": v(-0.26, 10.54) * mm, "end": v(-0.38, 10.73) * mm});
            skLineSegment(sketch, "E291", {"start": v(-0.38, 10.73) * mm, "end": v(-0.52, 10.94) * mm});
            skLineSegment(sketch, "E292", {"start": v(-0.52, 10.94) * mm, "end": v(-0.67, 11.15) * mm});
            skLineSegment(sketch, "E293", {"start": v(-0.67, 11.15) * mm, "end": v(-0.85, 11.37) * mm});
            skLineSegment(sketch, "E294", {"start": v(-0.85, 11.37) * mm, "end": v(-1.04, 11.6) * mm});
            skLineSegment(sketch, "E295", {"start": v(-1.04, 11.6) * mm, "end": v(-1.26, 11.82) * mm});
            skLineSegment(sketch, "E296", {"start": v(-1.26, 11.82) * mm, "end": v(-1.5, 12.05) * mm});
            skLineSegment(sketch, "E297", {"start": v(-1.5, 12.05) * mm, "end": v(-1.77, 12.29) * mm});
            skLineSegment(sketch, "E298", {"start": v(-1.77, 12.29) * mm, "end": v(-2.02, 12.34) * mm});
            skLineSegment(sketch, "E299", {"start": v(-2.02, 12.34) * mm, "end": v(-2.73, 12.2) * mm});
            skLineSegment(sketch, "E300", {"start": v(-2.73, 12.2) * mm, "end": v(-2.95, 12.06) * mm});
            skLineSegment(sketch, "E301", {"start": v(-2.95, 12.06) * mm, "end": v(-3.11, 11.74) * mm});
            skLineSegment(sketch, "E302", {"start": v(-3.11, 11.74) * mm, "end": v(-3.25, 11.44) * mm});
            skLineSegment(sketch, "E303", {"start": v(-3.25, 11.44) * mm, "end": v(-3.36, 11.14) * mm});
            skLineSegment(sketch, "E304", {"start": v(-3.36, 11.14) * mm, "end": v(-3.46, 10.86) * mm});
            skLineSegment(sketch, "E305", {"start": v(-3.46, 10.86) * mm, "end": v(-3.54, 10.6) * mm});
            skLineSegment(sketch, "E306", {"start": v(-3.54, 10.6) * mm, "end": v(-3.6, 10.34) * mm});
            skLineSegment(sketch, "E307", {"start": v(-3.6, 10.34) * mm, "end": v(-3.66, 10.1) * mm});
            skLineSegment(sketch, "E308", {"start": v(-3.66, 10.1) * mm, "end": v(-3.7, 9.87) * mm});
            skLineSegment(sketch, "E309", {"start": v(-3.7, 9.87) * mm, "end": v(-3.72, 9.67) * mm});
            skLineSegment(sketch, "E310", {"start": v(-3.72, 9.67) * mm, "end": v(-3.73, 9.47) * mm});
            skLineSegment(sketch, "E311", {"start": v(-3.73, 9.47) * mm, "end": v(-3.74, 9.3) * mm});
            skLineSegment(sketch, "E312", {"start": v(-3.74, 9.3) * mm, "end": v(-3.73, 9.14) * mm});
            skLineSegment(sketch, "E313", {"start": v(-3.73, 9.14) * mm, "end": v(-3.73, 9) * mm});
            skLineSegment(sketch, "E314", {"start": v(-3.73, 9) * mm, "end": v(-3.71, 8.88) * mm});
            skLineSegment(sketch, "E315", {"start": v(-3.71, 8.88) * mm, "end": v(-3.7, 8.78) * mm});
            skLineSegment(sketch, "E316", {"start": v(-3.7, 8.78) * mm, "end": v(-3.68, 8.7) * mm});
            skLineSegment(sketch, "E317", {"start": v(-3.68, 8.7) * mm, "end": v(-3.67, 8.63) * mm});
            skLineSegment(sketch, "E318", {"start": v(-3.67, 8.63) * mm, "end": v(-3.65, 8.58) * mm});
            skLineSegment(sketch, "E319", {"start": v(-3.65, 8.58) * mm, "end": v(-3.64, 8.55) * mm});
            skLineSegment(sketch, "E320", {"start": v(-3.64, 8.55) * mm, "end": v(-3.64, 8.53) * mm});
            skLineSegment(sketch, "E321", {"start": v(-3.64, 8.53) * mm, "end": v(-2.8, 6.55) * mm});
            skLineSegment(sketch, "E322", {"start": v(-2.8, 6.55) * mm, "end": v(-4.94, 5.14) * mm});
            skLineSegment(sketch, "E323", {"start": v(-4.94, 5.14) * mm, "end": v(-6.42, 6.69) * mm});
            skLineSegment(sketch, "E324", {"start": v(-6.42, 6.69) * mm, "end": v(-6.44, 6.7) * mm});
            skLineSegment(sketch, "E325", {"start": v(-6.44, 6.7) * mm, "end": v(-6.46, 6.72) * mm});
            skLineSegment(sketch, "E326", {"start": v(-6.46, 6.72) * mm, "end": v(-6.5, 6.75) * mm});
            skLineSegment(sketch, "E327", {"start": v(-6.5, 6.75) * mm, "end": v(-6.56, 6.8) * mm});
            skLineSegment(sketch, "E328", {"start": v(-6.56, 6.8) * mm, "end": v(-6.63, 6.84) * mm});
            skLineSegment(sketch, "E329", {"start": v(-6.63, 6.84) * mm, "end": v(-6.72, 6.9) * mm});
            skLineSegment(sketch, "E330", {"start": v(-6.72, 6.9) * mm, "end": v(-6.82, 6.95) * mm});
            skLineSegment(sketch, "E331", {"start": v(-6.82, 6.95) * mm, "end": v(-6.95, 7.02) * mm});
            skLineSegment(sketch, "E332", {"start": v(-6.95, 7.02) * mm, "end": v(-7.1, 7.08) * mm});
            skLineSegment(sketch, "E333", {"start": v(-7.1, 7.08) * mm, "end": v(-7.25, 7.14) * mm});
            skLineSegment(sketch, "E334", {"start": v(-7.25, 7.14) * mm, "end": v(-7.44, 7.2) * mm});
            skLineSegment(sketch, "E335", {"start": v(-7.44, 7.2) * mm, "end": v(-7.64, 7.27) * mm});
            skLineSegment(sketch, "E336", {"start": v(-7.64, 7.27) * mm, "end": v(-7.86, 7.32) * mm});
            skLineSegment(sketch, "E337", {"start": v(-7.86, 7.32) * mm, "end": v(-8.1, 7.37) * mm});
            skLineSegment(sketch, "E338", {"start": v(-8.1, 7.37) * mm, "end": v(-8.36, 7.4) * mm});
            skLineSegment(sketch, "E339", {"start": v(-8.36, 7.4) * mm, "end": v(-8.64, 7.44) * mm});
            skLineSegment(sketch, "E340", {"start": v(-8.64, 7.44) * mm, "end": v(-8.94, 7.46) * mm});
            skLineSegment(sketch, "E341", {"start": v(-8.94, 7.46) * mm, "end": v(-9.25, 7.47) * mm});
            skLineSegment(sketch, "E342", {"start": v(-9.25, 7.47) * mm, "end": v(-9.59, 7.46) * mm});
            skLineSegment(sketch, "E343", {"start": v(-9.59, 7.46) * mm, "end": v(-9.94, 7.44) * mm});
            skLineSegment(sketch, "E344", {"start": v(-9.94, 7.44) * mm, "end": v(-10.15, 7.3) * mm});
            skLineSegment(sketch, "E345", {"start": v(-10.15, 7.3) * mm, "end": v(-10.56, 6.7) * mm});
            skLineSegment(sketch, "E346", {"start": v(-10.56, 6.7) * mm, "end": v(-10.61, 6.44) * mm});
            skLineSegment(sketch, "E347", {"start": v(-10.61, 6.44) * mm, "end": v(-10.5, 6.1) * mm});
            skLineSegment(sketch, "E348", {"start": v(-10.5, 6.1) * mm, "end": v(-10.38, 5.8) * mm});
            skLineSegment(sketch, "E349", {"start": v(-10.38, 5.8) * mm, "end": v(-10.26, 5.5) * mm});
            skLineSegment(sketch, "E350", {"start": v(-10.26, 5.5) * mm, "end": v(-10.13, 5.23) * mm});
            skLineSegment(sketch, "E351", {"start": v(-10.13, 5.23) * mm, "end": v(-10, 4.99) * mm});
            skLineSegment(sketch, "E352", {"start": v(-10, 4.99) * mm, "end": v(-9.86, 4.76) * mm});
            skLineSegment(sketch, "E353", {"start": v(-9.86, 4.76) * mm, "end": v(-9.73, 4.56) * mm});
            skLineSegment(sketch, "E354", {"start": v(-9.73, 4.56) * mm, "end": v(-9.6, 4.37) * mm});
            skLineSegment(sketch, "E355", {"start": v(-9.6, 4.37) * mm, "end": v(-9.46, 4.2) * mm});
            skLineSegment(sketch, "E356", {"start": v(-9.46, 4.2) * mm, "end": v(-9.34, 4.06) * mm});
            skLineSegment(sketch, "E357", {"start": v(-9.34, 4.06) * mm, "end": v(-9.22, 3.93) * mm});
            skLineSegment(sketch, "E358", {"start": v(-9.22, 3.93) * mm, "end": v(-9.1, 3.82) * mm});
            skLineSegment(sketch, "E359", {"start": v(-9.1, 3.82) * mm, "end": v(-9, 3.73) * mm});
            skLineSegment(sketch, "E360", {"start": v(-9, 3.73) * mm, "end": v(-8.9, 3.65) * mm});
            skLineSegment(sketch, "E361", {"start": v(-8.9, 3.65) * mm, "end": v(-8.82, 3.6) * mm});
            skLineSegment(sketch, "E362", {"start": v(-8.82, 3.6) * mm, "end": v(-8.75, 3.54) * mm});
            skLineSegment(sketch, "E363", {"start": v(-8.75, 3.54) * mm, "end": v(-8.7, 3.5) * mm});
            skLineSegment(sketch, "E364", {"start": v(-8.7, 3.5) * mm, "end": v(-8.65, 3.48) * mm});
            skLineSegment(sketch, "E365", {"start": v(-8.65, 3.48) * mm, "end": v(-8.62, 3.47) * mm});
            skLineSegment(sketch, "E366", {"start": v(-8.62, 3.47) * mm, "end": v(-8.6, 3.46) * mm});
            skLineSegment(sketch, "E367", {"start": v(-8.6, 3.46) * mm, "end": v(-6.61, 2.66) * mm});
            skLineSegment(sketch, "E368", {"start": v(-6.61, 2.66) * mm, "end": v(-7.12, 0.14) * mm});
            skCircle(sketch, "E369", {"center": v(0, 0) * mm, "radius": 10 * mm, "construction": true});
            skSolve(sketch);
        }
        {
            var Q0;
            Q0 = qSketchRegion(id + "F0", true);
            extrude(context, id + "F1", {"entities" : qUnion([Q0]), "depth" : 10 * mm, "offsetDistance" : 25 * mm});
        }
    });
